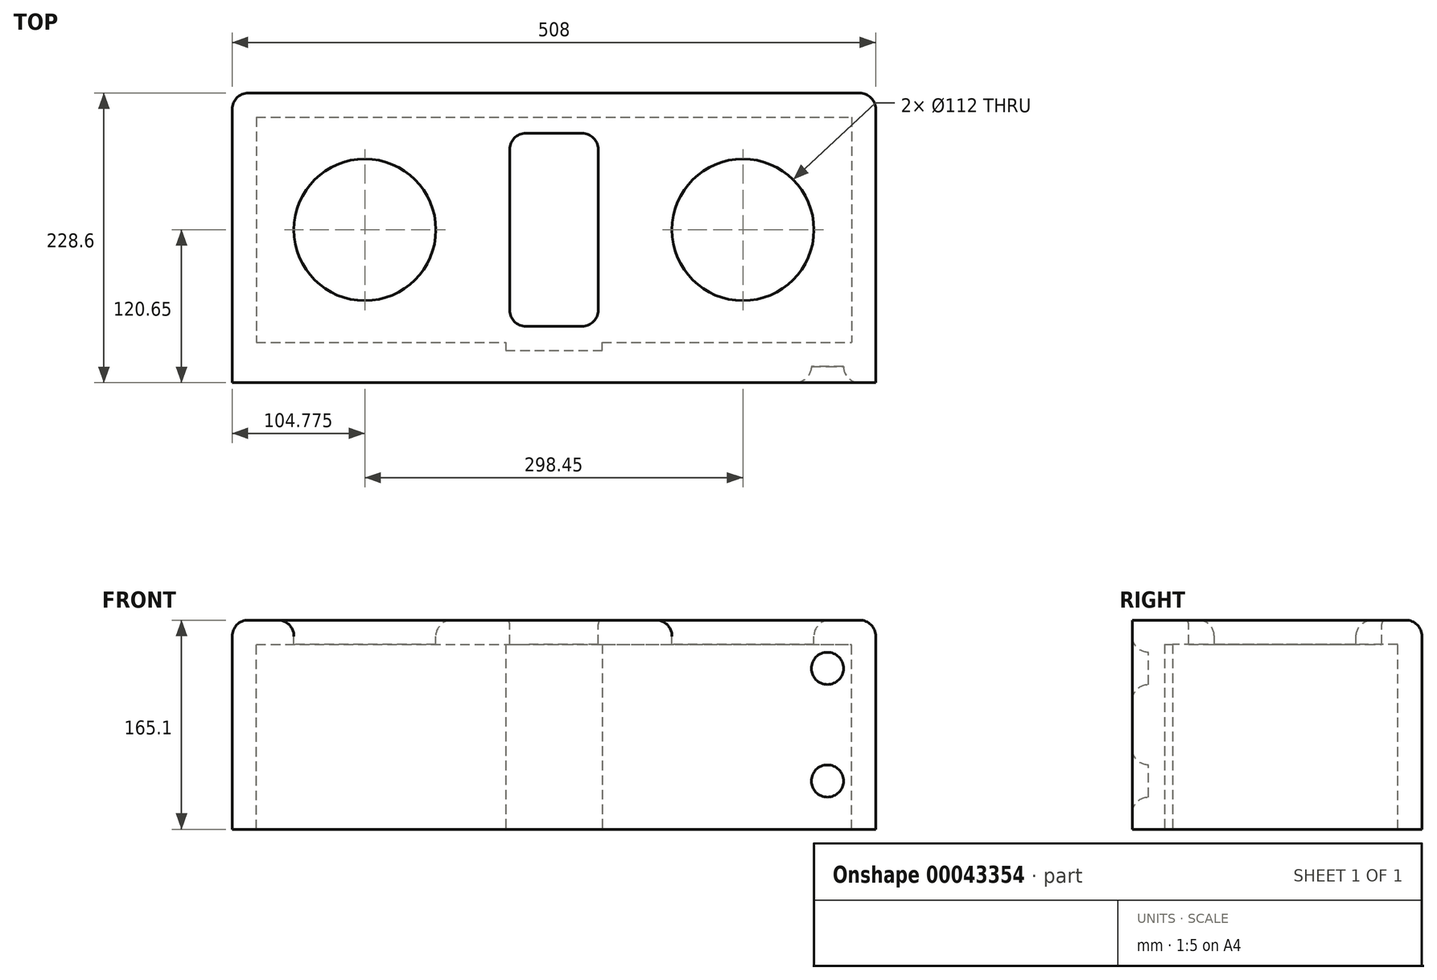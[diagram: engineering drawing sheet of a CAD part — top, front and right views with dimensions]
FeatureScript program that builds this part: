
annotation { "Feature Type Name" : "Feature", "Feature Type Description" : "" }
export const myFeature = defineFeature(function(context is Context, id is Id, definition is map)
    precondition{}
    {
        {
            var Q0;
            Q0=qCreatedBy(makeId("Top.planeOp"),FACE);
            var sketch = newSketch(context, id + "F0", { "sketchPlane" : qUnion([Q0])});
            skLineSegment(sketch, "E0.rect.bottom", {"start": v(254, -107.95) * mm, "end": v(-254, -107.95) * mm});
            skLineSegment(sketch, "E0.rect.top", {"start": v(254, 107.95) * mm, "end": v(-254, 107.95) * mm});
            skLineSegment(sketch, "E0.rect.left", {"start": v(254, -107.95) * mm, "end": v(254, 107.95) * mm});
            skLineSegment(sketch, "E0.rect.right", {"start": v(-254, -107.95) * mm, "end": v(-254, 107.95) * mm});
            skPoint(sketch, "E0.rect.middle", {"position": v(0, 0) * mm});
            skLineSegment(sketch, "E1.rect.bottom", {"start": v(38.1, -88.9) * mm, "end": v(-38.1, -88.9) * mm});
            skLineSegment(sketch, "E1.rect.top", {"start": v(38.1, 88.9) * mm, "end": v(-38.1, 88.9) * mm});
            skLineSegment(sketch, "E1.rect.left", {"start": v(38.1, -88.9) * mm, "end": v(38.1, 88.9) * mm});
            skLineSegment(sketch, "E1.rect.right", {"start": v(-38.1, -88.9) * mm, "end": v(-38.1, 88.9) * mm});
            skLineSegment(sketch, "E2.rect.bottom", {"start": v(22.22, -76.2) * mm, "end": v(-22.22, -76.2) * mm});
            skLineSegment(sketch, "E2.rect.top", {"start": v(22.23, 76.2) * mm, "end": v(-22.22, 76.2) * mm});
            skLineSegment(sketch, "E2.rect.left", {"start": v(34.92, -63.5) * mm, "end": v(34.93, 63.5) * mm});
            skLineSegment(sketch, "E2.rect.right", {"start": v(-34.93, -63.5) * mm, "end": v(-34.92, 63.5) * mm});
            skLineSegment(sketch, "E3", {"start": v(234.95, 88.9) * mm, "end": v(234.95, -88.9) * mm});
            skLineSegment(sketch, "E4", {"start": v(-234.95, 88.9) * mm, "end": v(-234.95, -88.9) * mm});
            skLineSegment(sketch, "E5", {"start": v(-234.95, -88.9) * mm, "end": v(234.95, -88.9) * mm});
            skLineSegment(sketch, "E6", {"start": v(-234.95, 88.9) * mm, "end": v(234.95, 88.9) * mm});
            skCircle(sketch, "E7", {"center": v(149.22, 0) * mm, "radius": 56 * mm});
            skCircle(sketch, "E8", {"center": v(-149.22, 0) * mm, "radius": 56 * mm});
            skPoint(sketch, "E9.visualSharp", {"position": v(-34.92, 76.2) * mm});
            skArc(sketch, "E9.filletArc", {"start": v(-22.22, 76.2) * mm, "mid": v(-31.2, 72.48) * mm, "end": v(-34.92, 63.5) * mm});
            skPoint(sketch, "E10.visualSharp", {"position": v(34.93, 76.2) * mm});
            skArc(sketch, "E10.filletArc", {"start": v(34.93, 63.5) * mm, "mid": v(31.2, 72.48) * mm, "end": v(22.23, 76.2) * mm});
            skPoint(sketch, "E11.visualSharp", {"position": v(34.92, -76.2) * mm});
            skArc(sketch, "E11.filletArc", {"start": v(22.22, -76.2) * mm, "mid": v(31.2, -72.48) * mm, "end": v(34.93, -63.5) * mm});
            skPoint(sketch, "E12.visualSharp", {"position": v(-34.93, -76.2) * mm});
            skArc(sketch, "E12.filletArc", {"start": v(-34.93, -63.5) * mm, "mid": v(-31.2, -72.48) * mm, "end": v(-22.22, -76.2) * mm});
            skSolve(sketch);
        }
        {
            var Q0;
            Q0=makeQuery(id+"F0.imprint","IMPRINT",FACE,{"disambiguationData":[TD([[makeQuery(id+"F0.imprint","IMPRINT",EDGE,{"derivedFrom":sQuery(id+"F0.wireOp",EDGE,"E0.rect.bottom")}),-1.0]])]});
            extrude(context, id + "F1", {"entities" : qUnion([Q0]), "oppositeDirection" : true, "depth" : 165.1 * mm});
        }
        {
            var Q0;
            {var subQ0=sQuery(id+"F0.wireOp",EDGE,"E1.rect.right");Q0=makeQuery(id+"F0.imprint","IMPRINT",FACE,{"disambiguationData":[TD([[makeQuery(id+"F0.imprint","IMPRINT",EDGE,{"derivedFrom":subQ0}),1.0]])]});}
            var Q1;
            {var subQ2=sQuery(id+"F0.wireOp",EDGE,"E1.rect.left");Q1=makeQuery(id+"F0.imprint","IMPRINT",FACE,{"disambiguationData":[TD([[makeQuery(id+"F0.imprint","IMPRINT",EDGE,{"derivedFrom":subQ2}),-1.0]])]});}
            var Q2;
            {var subQ2=sQuery(id+"F0.wireOp",EDGE,"E1.rect.left");Q2=makeQuery(id+"F0.imprint","IMPRINT",FACE,{"disambiguationData":[TD([[makeQuery(id+"F0.imprint","IMPRINT",EDGE,{"derivedFrom":subQ2}),1.0]])]});}
            extrude(context, id + "F2", {"entities" : qUnion([Q0, Q1, Q2]), "operationType" : NewBodyOperationType.ADD, "oppositeDirection" : true, "depth" : 19.05 * mm});
        }
        {
            var Q0;
            Q0=makeQuery(id+"F1.opExtrude","CAP_FACE",FACE,{"disambiguationData":[OSD([sQuery(id+"F0.wireOp",EDGE,"E0.rect.bottom"),sQuery(id+"F0.wireOp",EDGE,"E0.rect.top"),sQuery(id+"F0.wireOp",EDGE,"E0.rect.left"),sQuery(id+"F0.wireOp",EDGE,"E0.rect.right"),sQuery(id+"F0.wireOp",EDGE,"E3"),sQuery(id+"F0.wireOp",EDGE,"E4"),sQuery(id+"F0.wireOp",EDGE,"E5"),sQuery(id+"F0.wireOp",EDGE,"E6")])],"isStart":false});
            var sketch = newSketch(context, id + "F3", { "sketchPlane" : qUnion([Q0])});
            skLineSegment(sketch, "E13", {"start": v(0, -88.9) * mm, "end": v(38.1, -88.9) * mm});
            skLineSegment(sketch, "E14", {"start": v(38.1, -88.9) * mm, "end": v(38.1, -95.25) * mm});
            skLineSegment(sketch, "E15", {"start": v(38.1, -95.25) * mm, "end": v(-38.1, -95.25) * mm});
            skLineSegment(sketch, "E16", {"start": v(-38.1, -95.25) * mm, "end": v(-38.1, -88.9) * mm});
            skLineSegment(sketch, "E17", {"start": v(-38.1, -88.9) * mm, "end": v(0, -88.9) * mm});
            skLineSegment(sketch, "E18", {"start": v(0, 88.9) * mm, "end": v(-38.1, 88.9) * mm});
            skLineSegment(sketch, "E19", {"start": v(-38.1, 88.9) * mm, "end": v(-38.1, 95.25) * mm});
            skLineSegment(sketch, "E20", {"start": v(-38.1, 95.25) * mm, "end": v(38.1, 95.25) * mm});
            skLineSegment(sketch, "E21", {"start": v(38.1, 95.25) * mm, "end": v(38.1, 88.9) * mm});
            skLineSegment(sketch, "E22", {"start": v(38.1, 88.9) * mm, "end": v(0, 88.9) * mm});
            skSolve(sketch);
        }
        {
            var Q0;
            Q0=makeQuery(id+"F3.imprint","IMPRINT",FACE,{"disambiguationData":[TD([[makeQuery(id+"F3.imprint","IMPRINT",EDGE,{"derivedFrom":sQuery(id+"F3.wireOp",EDGE,"E18")}),1.0]])]});
            var Q1;
            Q1=makeQuery(id+"F3.imprint","IMPRINT",FACE,{"disambiguationData":[TD([[makeQuery(id+"F3.imprint","IMPRINT",EDGE,{"derivedFrom":sQuery(id+"F3.wireOp",EDGE,"E13")}),-1.0]])]});
            extrude(context, id + "F4", {"entities" : qUnion([Q0, Q1]), "operationType" : NewBodyOperationType.REMOVE, "oppositeDirection" : true, "depth" : 146.05 * mm});
        }
        {
            var Q0;
            Q0=makeQuery(id+"F2.opExtrude","CAP_EDGE",EDGE,{"disambiguationData":[OSD([sQuery(id+"F0.wireOp",EDGE,"E7")])],"isStart":true});
            var Q1;
            Q1=makeQuery(id+"F2.opExtrude","CAP_EDGE",EDGE,{"disambiguationData":[OSD([sQuery(id+"F0.wireOp",EDGE,"E8")])],"isStart":true});
            fillet(context, id + "F5", {"entities" : qUnion([Q0, Q1]), "radius" : 12.7 * mm, "tangentPropagation" : true, "allowEdgeOverflow" : false});
        }
        {
            var Q0;
            Q0=makeQuery(id+"F2.opExtrude","CAP_EDGE",EDGE,{"disambiguationData":[OSD([sQuery(id+"F0.wireOp",EDGE,"E2.rect.top")])],"isStart":true});
            fillet(context, id + "F6", {"entities" : qUnion([Q0]), "radius" : 3.17 * mm, "tangentPropagation" : true, "allowEdgeOverflow" : false});
        }
        {
            var Q0;
            Q0=makeQuery(id+"F1.opExtrude","SWEPT_FACE",FACE,{"disambiguationData":[OSD([sQuery(id+"F0.wireOp",EDGE,"E0.rect.bottom")])]});
            var sketch = newSketch(context, id + "F7", { "sketchPlane" : qUnion([Q0])});
            skCircle(sketch, "E23", {"center": v(-215.9, -38.1) * mm, "radius": 12.7 * mm});
            skCircle(sketch, "E24", {"center": v(-215.9, -127) * mm, "radius": 12.7 * mm});
            skCircle(sketch, "E25.MirrorC", {"center": v(215.9, -38.1) * mm, "radius": 12.7 * mm});
            skCircle(sketch, "E26.MirrorC", {"center": v(215.9, -127) * mm, "radius": 12.7 * mm});
            skPoint(sketch, "E27.start.orphan", {"position": v(0, -64.38) * mm});
            skSolve(sketch);
        }
        {
            var Q0;
            Q0=makeQuery(id+"F7.imprint","IMPRINT",FACE,{"disambiguationData":[TD([[makeQuery(id+"F7.imprint","IMPRINT",EDGE,{"derivedFrom":sQuery(id+"F7.wireOp",EDGE,"E23")}),1.0]])]});
            var Q1;
            Q1=makeQuery(id+"F7.imprint","IMPRINT",FACE,{"disambiguationData":[TD([[makeQuery(id+"F7.imprint","IMPRINT",EDGE,{"derivedFrom":sQuery(id+"F7.wireOp",EDGE,"E24")}),1.0]])]});
            var Q2;
            Q2=makeQuery(id+"F7.imprint","IMPRINT",FACE,{"disambiguationData":[TD([[makeQuery(id+"F7.imprint","IMPRINT",EDGE,{"derivedFrom":sQuery(id+"F7.wireOp",EDGE,"E25.MirrorC")}),-1.0]])]});
            var Q3;
            Q3=makeQuery(id+"F7.imprint","IMPRINT",FACE,{"disambiguationData":[TD([[makeQuery(id+"F7.imprint","IMPRINT",EDGE,{"derivedFrom":sQuery(id+"F7.wireOp",EDGE,"E26.MirrorC")}),-1.0]])]});
            extrude(context, id + "F8", {"entities" : qUnion([Q0, Q1, Q2, Q3]), "operationType" : NewBodyOperationType.ADD, "depth" : 12.7 * mm});
        }
        {
            var Q0;
            Q0=makeQuery(id+"F8.opExtrude","CAP_EDGE",EDGE,{"disambiguationData":[OSD([sQuery(id+"F7.wireOp",EDGE,"E24")])],"isStart":false});
            var Q1;
            Q1=makeQuery(id+"F8.opExtrude","CAP_EDGE",EDGE,{"disambiguationData":[OSD([sQuery(id+"F7.wireOp",EDGE,"E23")])],"isStart":false});
            var Q2;
            Q2=makeQuery(id+"F8.opExtrude","CAP_EDGE",EDGE,{"disambiguationData":[OSD([sQuery(id+"F7.wireOp",EDGE,"E25.MirrorC")])],"isStart":false});
            var Q3;
            Q3=makeQuery(id+"F8.opExtrude","CAP_EDGE",EDGE,{"disambiguationData":[OSD([sQuery(id+"F7.wireOp",EDGE,"E26.MirrorC")])],"isStart":false});
            fillet(context, id + "F9", {"entities" : qUnion([Q0, Q1, Q2, Q3]), "radius" : 12.7 * mm, "tangentPropagation" : true, "allowEdgeOverflow" : false});
        }
        {
            var Q0;
            Q0=makeQuery(id+"F1.opExtrude","SWEPT_EDGE",EDGE,{"disambiguationData":[OSD([sQuery(id+"F0.wireOp",EDGE,"E0.rect.top"),sQuery(id+"F0.wireOp",EDGE,"E0.rect.left")])]});
            var Q1;
            Q1=makeQuery(id+"F1.opExtrude","SWEPT_EDGE",EDGE,{"disambiguationData":[OSD([sQuery(id+"F0.wireOp",EDGE,"E0.rect.bottom"),sQuery(id+"F0.wireOp",EDGE,"E0.rect.left")])]});
            var Q2;
            Q2=makeQuery(id+"F1.opExtrude","SWEPT_EDGE",EDGE,{"disambiguationData":[OSD([sQuery(id+"F0.wireOp",EDGE,"E0.rect.bottom"),sQuery(id+"F0.wireOp",EDGE,"E0.rect.right")])]});
            var Q3;
            Q3=makeQuery(id+"F1.opExtrude","SWEPT_EDGE",EDGE,{"disambiguationData":[OSD([sQuery(id+"F0.wireOp",EDGE,"E0.rect.top"),sQuery(id+"F0.wireOp",EDGE,"E0.rect.right")])]});
            var Q4;
            Q4=makeQuery(id+"F1.opExtrude","CAP_EDGE",EDGE,{"disambiguationData":[OSD([sQuery(id+"F0.wireOp",EDGE,"E0.rect.left")])],"isStart":true});
            var Q5;
            Q5=makeQuery(id+"F1.opExtrude","CAP_EDGE",EDGE,{"disambiguationData":[OSD([sQuery(id+"F0.wireOp",EDGE,"E0.rect.top")])],"isStart":true});
            var Q6;
            Q6=makeQuery(id+"F1.opExtrude","CAP_EDGE",EDGE,{"disambiguationData":[OSD([sQuery(id+"F0.wireOp",EDGE,"E0.rect.bottom")])],"isStart":true});
            var Q7;
            Q7=makeQuery(id+"F1.opExtrude","CAP_EDGE",EDGE,{"disambiguationData":[OSD([sQuery(id+"F0.wireOp",EDGE,"E0.rect.right")])],"isStart":true});
            fillet(context, id + "F10", {"entities" : qUnion([Q0, Q1, Q2, Q3, Q4, Q5, Q6, Q7]), "radius" : 12.7 * mm, "tangentPropagation" : true, "allowEdgeOverflow" : false});
        }
    });
